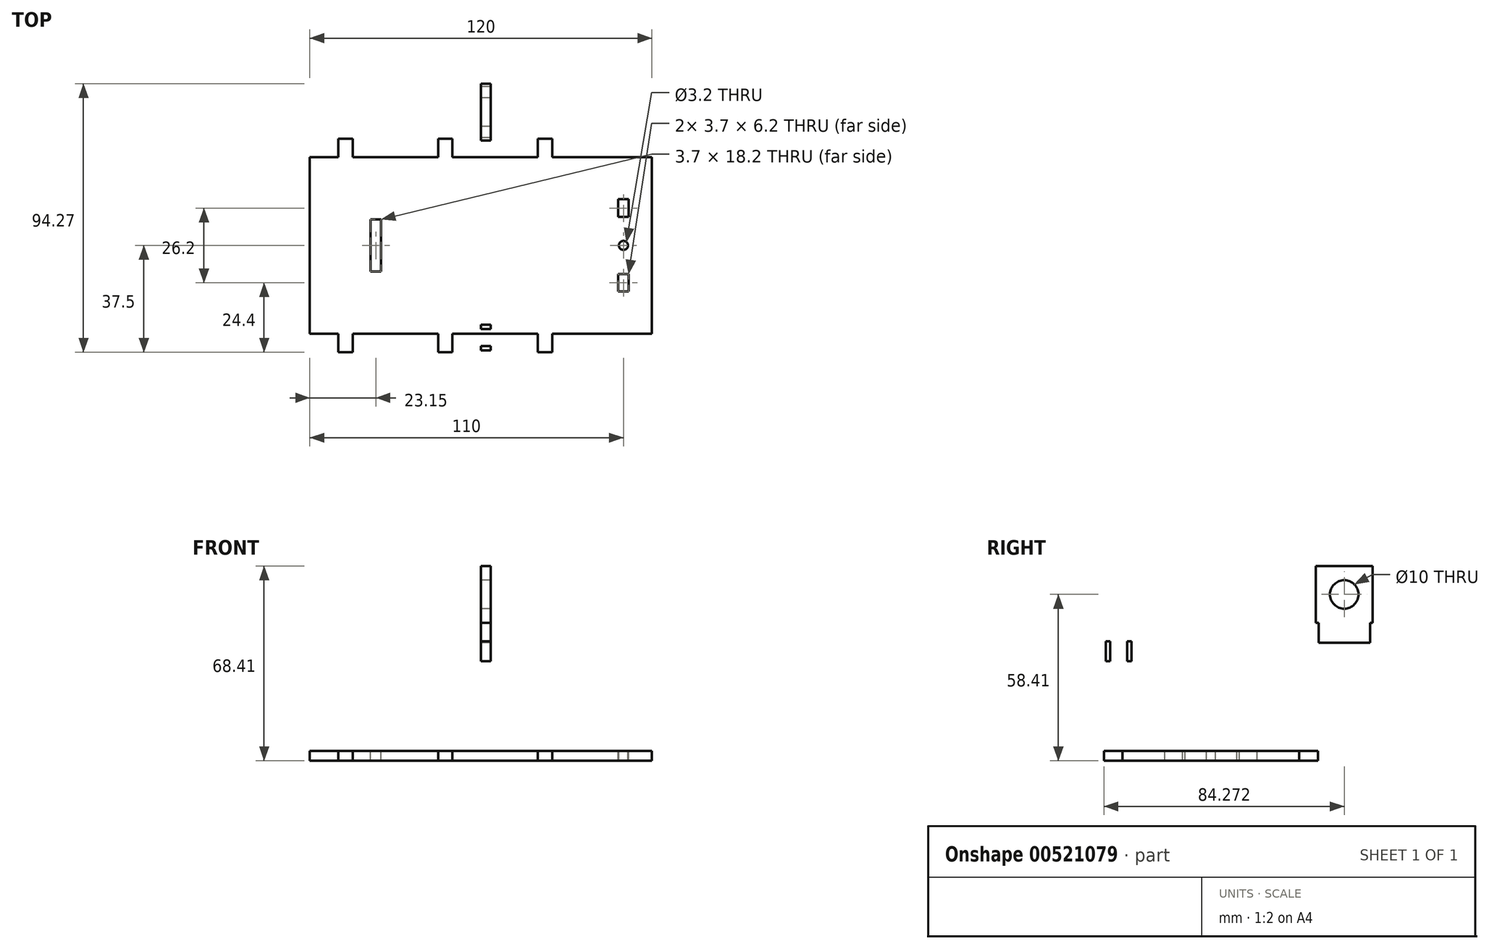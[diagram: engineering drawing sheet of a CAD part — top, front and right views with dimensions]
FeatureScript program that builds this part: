
annotation { "Feature Type Name" : "Feature", "Feature Type Description" : "" }
export const myFeature = defineFeature(function(context is Context, id is Id, definition is map)
    precondition{}
    {
        {
            var Q0;
            Q0=qCreatedBy(makeId("Top.planeOp"),FACE);
            var sketch = newSketch(context, id + "F0", { "sketchPlane" : qUnion([Q0])});
            skLineSegment(sketch, "E0.bottom", {"start": v(60, -31) * mm, "end": v(-60, -31) * mm});
            skLineSegment(sketch, "E0.top", {"start": v(60, 31) * mm, "end": v(-60, 31) * mm});
            skLineSegment(sketch, "E0.left", {"start": v(60, -31) * mm, "end": v(60, 31) * mm});
            skLineSegment(sketch, "E0.right", {"start": v(-60, -31) * mm, "end": v(-60, 31) * mm});
            skPoint(sketch, "E0.middle", {"position": v(0, 0) * mm});
            skSolve(sketch);
        }
        {
            var Q0;
            Q0 = qSketchRegion(id + "F0", true);
            extrude(context, id + "F1", {"entities" : qUnion([Q0]), "depth" : 3.5 * mm, "offsetDistance" : 25 * mm});
        }
        {
            var Q0;
            Q0=makeQuery(id+"F1.opExtrude","CAP_FACE",FACE,{"disambiguationData":[OSD([sQuery(id+"F0.wireOp",EDGE,"E0.bottom"),sQuery(id+"F0.wireOp",EDGE,"E0.top"),sQuery(id+"F0.wireOp",EDGE,"E0.left"),sQuery(id+"F0.wireOp",EDGE,"E0.right")])],"isStart":false});
            var sketch = newSketch(context, id + "F2", { "sketchPlane" : qUnion([Q0])});
            skLineSegment(sketch, "E1", {"start": v(-60, -31) * mm, "end": v(-50, -31) * mm});
            skLineSegment(sketch, "E2.bottom", {"start": v(-50, -31) * mm, "end": v(-45, -31) * mm});
            skLineSegment(sketch, "E2.top", {"start": v(-50, -37.5) * mm, "end": v(-45, -37.5) * mm});
            skLineSegment(sketch, "E2.left", {"start": v(-50, -31) * mm, "end": v(-50, -37.5) * mm});
            skLineSegment(sketch, "E2.right", {"start": v(-45, -31) * mm, "end": v(-45, -37.5) * mm});
            skLineSegment(sketch, "E3", {"start": v(-45, -31) * mm, "end": v(-15, -31) * mm});
            skLineSegment(sketch, "E4.bottom", {"start": v(-15, -31) * mm, "end": v(-10, -31) * mm});
            skLineSegment(sketch, "E4.top", {"start": v(-15, -37.5) * mm, "end": v(-10, -37.5) * mm});
            skLineSegment(sketch, "E4.left", {"start": v(-15, -31) * mm, "end": v(-15, -37.5) * mm});
            skLineSegment(sketch, "E4.right", {"start": v(-10, -31) * mm, "end": v(-10, -37.5) * mm});
            skLineSegment(sketch, "E5", {"start": v(-10, -31) * mm, "end": v(20, -31) * mm});
            skLineSegment(sketch, "E6.bottom", {"start": v(20, -31) * mm, "end": v(25, -31) * mm});
            skLineSegment(sketch, "E6.top", {"start": v(20, -37.5) * mm, "end": v(25, -37.5) * mm});
            skLineSegment(sketch, "E6.left", {"start": v(20, -31) * mm, "end": v(20, -37.5) * mm});
            skLineSegment(sketch, "E6.right", {"start": v(25, -31) * mm, "end": v(25, -37.5) * mm});
            skLineSegment(sketch, "E7", {"start": v(-60, 31) * mm, "end": v(-50, 31) * mm});
            skLineSegment(sketch, "E8.bottom", {"start": v(-50, 31) * mm, "end": v(-45, 31) * mm});
            skLineSegment(sketch, "E8.top", {"start": v(-50, 37.5) * mm, "end": v(-45, 37.5) * mm});
            skLineSegment(sketch, "E8.left", {"start": v(-50, 31) * mm, "end": v(-50, 37.5) * mm});
            skLineSegment(sketch, "E8.right", {"start": v(-45, 31) * mm, "end": v(-45, 37.5) * mm});
            skLineSegment(sketch, "E9", {"start": v(-45, 31) * mm, "end": v(-15, 31) * mm});
            skLineSegment(sketch, "E10.bottom", {"start": v(-15, 31) * mm, "end": v(-10, 31) * mm});
            skLineSegment(sketch, "E10.top", {"start": v(-15, 37.5) * mm, "end": v(-10, 37.5) * mm});
            skLineSegment(sketch, "E10.left", {"start": v(-15, 31) * mm, "end": v(-15, 37.5) * mm});
            skLineSegment(sketch, "E10.right", {"start": v(-10, 31) * mm, "end": v(-10, 37.5) * mm});
            skLineSegment(sketch, "E11", {"start": v(-10, 31) * mm, "end": v(20, 31) * mm});
            skLineSegment(sketch, "E12.bottom", {"start": v(20, 31) * mm, "end": v(25, 31) * mm});
            skLineSegment(sketch, "E12.top", {"start": v(20, 37.5) * mm, "end": v(25, 37.5) * mm});
            skLineSegment(sketch, "E12.left", {"start": v(20, 31) * mm, "end": v(20, 37.5) * mm});
            skLineSegment(sketch, "E12.right", {"start": v(25, 31) * mm, "end": v(25, 37.5) * mm});
            skSolve(sketch);
        }
        {
            var Q0;
            Q0=makeQuery(id+"F2.imprint","IMPRINT",FACE,{"disambiguationData":[TD([[makeQuery(id+"F2.imprint","IMPRINT",EDGE,{"derivedFrom":sQuery(id+"F2.wireOp",EDGE,"E8.bottom")}),-1.0]])]});
            var Q1;
            Q1=makeQuery(id+"F2.imprint","IMPRINT",FACE,{"disambiguationData":[TD([[makeQuery(id+"F2.imprint","IMPRINT",EDGE,{"derivedFrom":sQuery(id+"F2.wireOp",EDGE,"E10.bottom")}),-1.0]])]});
            var Q2;
            Q2=makeQuery(id+"F2.imprint","IMPRINT",FACE,{"disambiguationData":[TD([[makeQuery(id+"F2.imprint","IMPRINT",EDGE,{"derivedFrom":sQuery(id+"F2.wireOp",EDGE,"E12.bottom")}),-1.0]])]});
            var Q3;
            Q3=makeQuery(id+"F2.imprint","IMPRINT",FACE,{"disambiguationData":[TD([[makeQuery(id+"F2.imprint","IMPRINT",EDGE,{"derivedFrom":sQuery(id+"F2.wireOp",EDGE,"E2.bottom")}),1.0]])]});
            var Q4;
            Q4=makeQuery(id+"F2.imprint","IMPRINT",FACE,{"disambiguationData":[TD([[makeQuery(id+"F2.imprint","IMPRINT",EDGE,{"derivedFrom":sQuery(id+"F2.wireOp",EDGE,"E4.bottom")}),1.0]])]});
            var Q5;
            Q5=makeQuery(id+"F2.imprint","IMPRINT",FACE,{"disambiguationData":[TD([[makeQuery(id+"F2.imprint","IMPRINT",EDGE,{"derivedFrom":sQuery(id+"F2.wireOp",EDGE,"E6.bottom")}),1.0]])]});
            extrude(context, id + "F3", {"entities" : qUnion([Q0, Q1, Q2, Q3, Q4, Q5]), "operationType" : NewBodyOperationType.ADD, "oppositeDirection" : true, "depth" : 3.5 * mm, "offsetDistance" : 25 * mm});
        }
        {
            var Q0;
            Q0=makeQuery(id+"F3.boolean.opBoolean","MERGE",FACE,{"derivedFrom":[makeQuery(id+"F1.opExtrude","CAP_FACE",FACE,{"disambiguationData":[OSD([sQuery(id+"F0.wireOp",EDGE,"E0.bottom"),sQuery(id+"F0.wireOp",EDGE,"E0.top"),sQuery(id+"F0.wireOp",EDGE,"E0.left"),sQuery(id+"F0.wireOp",EDGE,"E0.right")])],"isStart":false}),makeQuery(id+"F3.opExtrude","CAP_FACE",FACE,{"disambiguationData":[OSD([sQuery(id+"F2.wireOp",EDGE,"E2.bottom"),sQuery(id+"F2.wireOp",EDGE,"E2.top"),sQuery(id+"F2.wireOp",EDGE,"E2.left"),sQuery(id+"F2.wireOp",EDGE,"E2.right")])],"isStart":true}),makeQuery(id+"F3.opExtrude","CAP_FACE",FACE,{"disambiguationData":[OSD([sQuery(id+"F2.wireOp",EDGE,"E4.bottom"),sQuery(id+"F2.wireOp",EDGE,"E4.top"),sQuery(id+"F2.wireOp",EDGE,"E4.left"),sQuery(id+"F2.wireOp",EDGE,"E4.right")])],"isStart":true}),makeQuery(id+"F3.opExtrude","CAP_FACE",FACE,{"disambiguationData":[OSD([sQuery(id+"F2.wireOp",EDGE,"E6.bottom"),sQuery(id+"F2.wireOp",EDGE,"E6.top"),sQuery(id+"F2.wireOp",EDGE,"E6.left"),sQuery(id+"F2.wireOp",EDGE,"E6.right")])],"isStart":true}),makeQuery(id+"F3.opExtrude","CAP_FACE",FACE,{"disambiguationData":[OSD([sQuery(id+"F2.wireOp",EDGE,"E8.bottom"),sQuery(id+"F2.wireOp",EDGE,"E8.top"),sQuery(id+"F2.wireOp",EDGE,"E8.left"),sQuery(id+"F2.wireOp",EDGE,"E8.right")])],"isStart":true}),makeQuery(id+"F3.opExtrude","CAP_FACE",FACE,{"disambiguationData":[OSD([sQuery(id+"F2.wireOp",EDGE,"E10.bottom"),sQuery(id+"F2.wireOp",EDGE,"E10.top"),sQuery(id+"F2.wireOp",EDGE,"E10.left"),sQuery(id+"F2.wireOp",EDGE,"E10.right")])],"isStart":true}),makeQuery(id+"F3.opExtrude","CAP_FACE",FACE,{"disambiguationData":[OSD([sQuery(id+"F2.wireOp",EDGE,"E12.bottom"),sQuery(id+"F2.wireOp",EDGE,"E12.top"),sQuery(id+"F2.wireOp",EDGE,"E12.left"),sQuery(id+"F2.wireOp",EDGE,"E12.right")])],"isStart":true})]});
            var sketch = newSketch(context, id + "F4", { "sketchPlane" : qUnion([Q0])});
            skLineSegment(sketch, "E13", {"start": v(60, 0) * mm, "end": v(50, 0) * mm});
            skCircle(sketch, "E14", {"center": v(50, 0) * mm, "radius": 1.6 * mm});
            skSolve(sketch);
        }
        {
            var Q0;
            Q0=makeQuery(id+"F4.imprint","IMPRINT",FACE,{"disambiguationData":[TD([[makeQuery(id+"F4.imprint","IMPRINT",EDGE,{"derivedFrom":sQuery(id+"F4.wireOp",EDGE,"E14")}),1.0]])]});
            extrude(context, id + "F5", {"entities" : qUnion([Q0]), "operationType" : NewBodyOperationType.REMOVE, "endBound" : BoundingType.THROUGH_ALL, "oppositeDirection" : true, "depth" : 25 * mm, "offsetDistance" : 25 * mm});
        }
        {
            var Q0;
            Q0=makeQuery(id+"F3.boolean.opBoolean","MERGE",FACE,{"derivedFrom":[makeQuery(id+"F1.opExtrude","CAP_FACE",FACE,{"disambiguationData":[OSD([sQuery(id+"F0.wireOp",EDGE,"E0.bottom"),sQuery(id+"F0.wireOp",EDGE,"E0.top"),sQuery(id+"F0.wireOp",EDGE,"E0.left"),sQuery(id+"F0.wireOp",EDGE,"E0.right")])],"isStart":false}),makeQuery(id+"F3.opExtrude","CAP_FACE",FACE,{"disambiguationData":[OSD([sQuery(id+"F2.wireOp",EDGE,"E2.bottom"),sQuery(id+"F2.wireOp",EDGE,"E2.top"),sQuery(id+"F2.wireOp",EDGE,"E2.left"),sQuery(id+"F2.wireOp",EDGE,"E2.right")])],"isStart":true}),makeQuery(id+"F3.opExtrude","CAP_FACE",FACE,{"disambiguationData":[OSD([sQuery(id+"F2.wireOp",EDGE,"E4.bottom"),sQuery(id+"F2.wireOp",EDGE,"E4.top"),sQuery(id+"F2.wireOp",EDGE,"E4.left"),sQuery(id+"F2.wireOp",EDGE,"E4.right")])],"isStart":true}),makeQuery(id+"F3.opExtrude","CAP_FACE",FACE,{"disambiguationData":[OSD([sQuery(id+"F2.wireOp",EDGE,"E6.bottom"),sQuery(id+"F2.wireOp",EDGE,"E6.top"),sQuery(id+"F2.wireOp",EDGE,"E6.left"),sQuery(id+"F2.wireOp",EDGE,"E6.right")])],"isStart":true}),makeQuery(id+"F3.opExtrude","CAP_FACE",FACE,{"disambiguationData":[OSD([sQuery(id+"F2.wireOp",EDGE,"E8.bottom"),sQuery(id+"F2.wireOp",EDGE,"E8.top"),sQuery(id+"F2.wireOp",EDGE,"E8.left"),sQuery(id+"F2.wireOp",EDGE,"E8.right")])],"isStart":true}),makeQuery(id+"F3.opExtrude","CAP_FACE",FACE,{"disambiguationData":[OSD([sQuery(id+"F2.wireOp",EDGE,"E10.bottom"),sQuery(id+"F2.wireOp",EDGE,"E10.top"),sQuery(id+"F2.wireOp",EDGE,"E10.left"),sQuery(id+"F2.wireOp",EDGE,"E10.right")])],"isStart":true}),makeQuery(id+"F3.opExtrude","CAP_FACE",FACE,{"disambiguationData":[OSD([sQuery(id+"F2.wireOp",EDGE,"E12.bottom"),sQuery(id+"F2.wireOp",EDGE,"E12.top"),sQuery(id+"F2.wireOp",EDGE,"E12.left"),sQuery(id+"F2.wireOp",EDGE,"E12.right")])],"isStart":true})]});
            var sketch = newSketch(context, id + "F6", { "sketchPlane" : qUnion([Q0])});
            skLineSegment(sketch, "E15", {"start": v(60, 0) * mm, "end": v(50, 0) * mm});
            skLineSegment(sketch, "E16", {"start": v(50, 0) * mm, "end": v(-35, 0) * mm});
            skLineSegment(sketch, "E17", {"start": v(50, 10) * mm, "end": v(50, -10) * mm});
            skLineSegment(sketch, "E18.bottom", {"start": v(48.15, 10) * mm, "end": v(51.85, 10) * mm});
            skLineSegment(sketch, "E18.top", {"start": v(48.15, 16.2) * mm, "end": v(51.85, 16.2) * mm});
            skLineSegment(sketch, "E18.left", {"start": v(48.15, 10) * mm, "end": v(48.15, 16.2) * mm});
            skLineSegment(sketch, "E18.right", {"start": v(51.85, 10) * mm, "end": v(51.85, 16.2) * mm});
            skLineSegment(sketch, "E19.bottom", {"start": v(48.15, -10) * mm, "end": v(51.85, -10) * mm});
            skLineSegment(sketch, "E19.top", {"start": v(48.15, -16.2) * mm, "end": v(51.85, -16.2) * mm});
            skLineSegment(sketch, "E19.left", {"start": v(48.15, -10) * mm, "end": v(48.15, -16.2) * mm});
            skLineSegment(sketch, "E19.right", {"start": v(51.85, -10) * mm, "end": v(51.85, -16.2) * mm});
            skLineSegment(sketch, "E20.bottom", {"start": v(-35, -9.1) * mm, "end": v(-38.7, -9.1) * mm});
            skLineSegment(sketch, "E20.top", {"start": v(-35, 9.1) * mm, "end": v(-38.7, 9.1) * mm});
            skLineSegment(sketch, "E20.left", {"start": v(-35, -9.1) * mm, "end": v(-35, 9.1) * mm});
            skLineSegment(sketch, "E20.right", {"start": v(-38.7, -9.1) * mm, "end": v(-38.7, 9.1) * mm});
            skSolve(sketch);
        }
        {
            var Q0;
            {var subQ3=sQuery(id+"F6.wireOp",EDGE,"E20.bottom");Q0=makeQuery(id+"F6.imprint","IMPRINT",FACE,{"disambiguationData":[TD([[makeQuery(id+"F6.imprint","IMPRINT",EDGE,{"derivedFrom":subQ3}),-1.0]])]});}
            var Q1;
            Q1=makeQuery(id+"F6.imprint","IMPRINT",FACE,{"disambiguationData":[TD([[makeQuery(id+"F6.imprint","IMPRINT",EDGE,{"derivedFrom":sQuery(id+"F6.wireOp",EDGE,"E18.top")}),-1.0]])]});
            var Q2;
            Q2=makeQuery(id+"F6.imprint","IMPRINT",FACE,{"disambiguationData":[TD([[makeQuery(id+"F6.imprint","IMPRINT",EDGE,{"derivedFrom":sQuery(id+"F6.wireOp",EDGE,"E19.top")}),1.0]])]});
            extrude(context, id + "F7", {"entities" : qUnion([Q0, Q1, Q2]), "operationType" : NewBodyOperationType.REMOVE, "endBound" : BoundingType.THROUGH_ALL, "oppositeDirection" : true, "depth" : 100 * mm, "offsetDistance" : 25 * mm});
        }
        {
            var Q0;
            Q0=qCreatedBy(makeId("Right.planeOp"),FACE);
            var sketch = newSketch(context, id + "F8", { "sketchPlane" : qUnion([Q0])});
            skLineSegment(sketch, "E21.bottom", {"start": v(-36.87, 34.95) * mm, "end": v(-27.87, 34.95) * mm});
            skLineSegment(sketch, "E21.top", {"start": v(-36.87, 64.95) * mm, "end": v(-27.87, 64.95) * mm});
            skLineSegment(sketch, "E21.left", {"start": v(-36.87, 34.95) * mm, "end": v(-36.87, 64.95) * mm});
            skLineSegment(sketch, "E21.right", {"start": v(-27.87, 34.95) * mm, "end": v(-27.87, 64.95) * mm});
            skLineSegment(sketch, "E22.bottom", {"start": v(-36.87, 34.95) * mm, "end": v(-35.37, 34.95) * mm});
            skLineSegment(sketch, "E22.top", {"start": v(-36.87, 41.95) * mm, "end": v(-35.37, 41.95) * mm});
            skLineSegment(sketch, "E22.left", {"start": v(-36.87, 34.95) * mm, "end": v(-36.87, 41.95) * mm});
            skLineSegment(sketch, "E22.right", {"start": v(-35.37, 34.95) * mm, "end": v(-35.37, 41.95) * mm});
            skLineSegment(sketch, "E23.bottom", {"start": v(-27.87, 34.95) * mm, "end": v(-29.37, 34.95) * mm});
            skLineSegment(sketch, "E23.top", {"start": v(-27.87, 41.95) * mm, "end": v(-29.37, 41.95) * mm});
            skLineSegment(sketch, "E23.left", {"start": v(-27.87, 34.95) * mm, "end": v(-27.87, 41.95) * mm});
            skLineSegment(sketch, "E23.right", {"start": v(-29.37, 34.95) * mm, "end": v(-29.37, 41.95) * mm});
            skSolve(sketch);
        }
        {
            var Q0;
            Q0=makeQuery(id+"F8.imprint","IMPRINT",FACE,{"disambiguationData":[TD([[makeQuery(id+"F8.imprint","IMPRINT",EDGE,{"derivedFrom":sQuery(id+"F8.wireOp",EDGE,"E21.bottom")}),1.0]])]});
            extrude(context, id + "F9", {"entities" : qUnion([Q0]), "depth" : 3.5 * mm, "offsetDistance" : 25 * mm});
        }
        {
            var Q0;
            Q0=qCreatedBy(makeId("Right.planeOp"),FACE);
            var sketch = newSketch(context, id + "F10", { "sketchPlane" : qUnion([Q0])});
            skLineSegment(sketch, "E24.bottom", {"start": v(36.77, 41.4) * mm, "end": v(56.77, 41.4) * mm});
            skLineSegment(sketch, "E24.top", {"start": v(36.77, 68.4) * mm, "end": v(56.77, 68.4) * mm});
            skLineSegment(sketch, "E24.left", {"start": v(36.77, 41.4) * mm, "end": v(36.77, 68.4) * mm});
            skLineSegment(sketch, "E24.right", {"start": v(56.77, 41.4) * mm, "end": v(56.77, 68.4) * mm});
            skLineSegment(sketch, "E25.bottom", {"start": v(36.77, 41.4) * mm, "end": v(37.77, 41.4) * mm});
            skLineSegment(sketch, "E25.top", {"start": v(36.77, 48.4) * mm, "end": v(37.77, 48.4) * mm});
            skLineSegment(sketch, "E25.left", {"start": v(36.77, 41.4) * mm, "end": v(36.77, 48.4) * mm});
            skLineSegment(sketch, "E25.right", {"start": v(37.77, 41.4) * mm, "end": v(37.77, 48.4) * mm});
            skLineSegment(sketch, "E26.bottom", {"start": v(56.77, 41.4) * mm, "end": v(55.77, 41.4) * mm});
            skLineSegment(sketch, "E26.top", {"start": v(56.77, 48.4) * mm, "end": v(55.77, 48.4) * mm});
            skLineSegment(sketch, "E26.left", {"start": v(56.77, 41.4) * mm, "end": v(56.77, 48.4) * mm});
            skLineSegment(sketch, "E26.right", {"start": v(55.77, 41.4) * mm, "end": v(55.77, 48.4) * mm});
            skLineSegment(sketch, "E27", {"start": v(46.77, 41.4) * mm, "end": v(46.77, 58.4) * mm});
            skCircle(sketch, "E28", {"center": v(46.77, 58.4) * mm, "radius": 5 * mm});
            skSolve(sketch);
        }
        {
            var Q0;
            Q0=makeQuery(id+"F10.imprint","IMPRINT",FACE,{"disambiguationData":[TD([[makeQuery(id+"F10.imprint","IMPRINT",EDGE,{"derivedFrom":sQuery(id+"F10.wireOp",EDGE,"E24.top")}),-1.0]])]});
            extrude(context, id + "F11", {"entities" : qUnion([Q0]), "depth" : 3.5 * mm, "offsetDistance" : 25 * mm});
        }
    });
